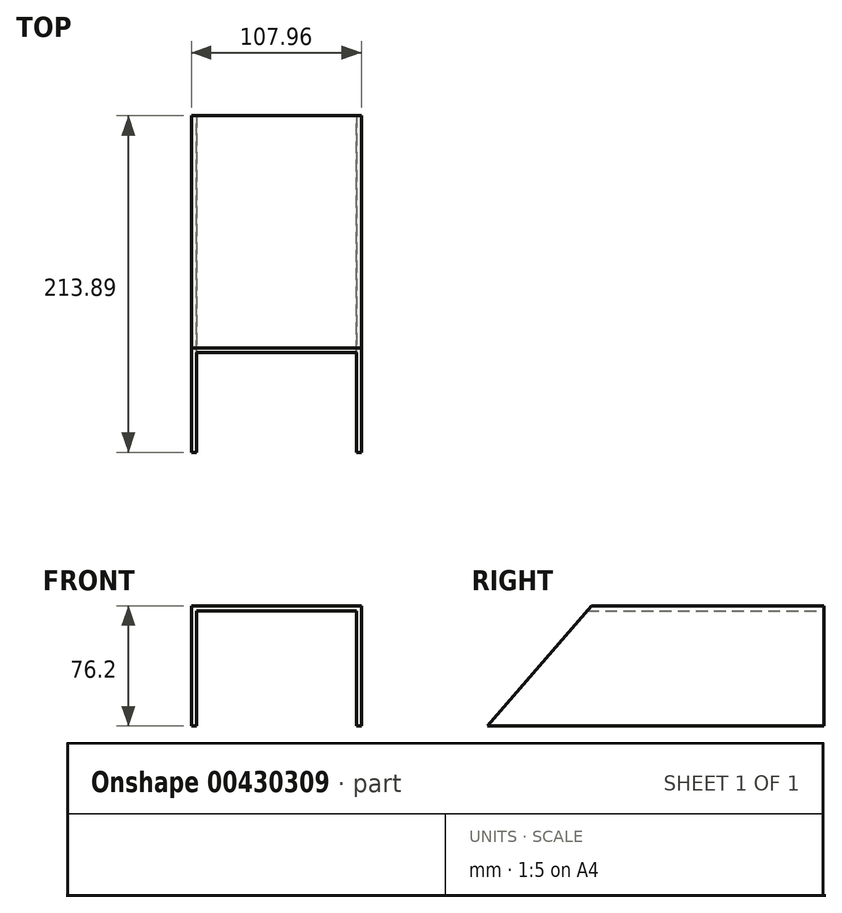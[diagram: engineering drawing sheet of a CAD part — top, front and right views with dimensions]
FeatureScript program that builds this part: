
annotation { "Feature Type Name" : "Feature", "Feature Type Description" : "" }
export const myFeature = defineFeature(function(context is Context, id is Id, definition is map)
    precondition{}
    {
        {
            var Q0;
            Q0=qCreatedBy(makeId("Right.planeOp"),FACE);
            cPlane(context, id + "F0", {"entities" : qUnion([Q0]), "cplaneType" : CPlaneType.OFFSET, "offset" : 50.8 * mm, "width" : 152.4 * mm, "height" : 152.4 * mm});
        }
        {
            var Q0;
            Q0=qCreatedBy(id+"F0.planeOp",FACE);
            var sketch = newSketch(context, id + "F1", { "sketchPlane" : qUnion([Q0])});
            skLineSegment(sketch, "E0", {"start": v(-134.55, 0) * mm, "end": v(-68.29, 76.2) * mm});
            skLineSegment(sketch, "E1", {"start": v(-68.29, 76.2) * mm, "end": v(79.34, 76.2) * mm});
            skLineSegment(sketch, "E2", {"start": v(79.34, 76.2) * mm, "end": v(79.34, 0) * mm});
            skLineSegment(sketch, "E3", {"start": v(79.34, 0) * mm, "end": v(-134.55, 0) * mm});
            skSolve(sketch);
        }
        {
            var Q0;
            Q0=makeQuery(id+"F1.imprint","IMPRINT",FACE,{"disambiguationData":[TD([[makeQuery(id+"F1.imprint","IMPRINT",EDGE,{"derivedFrom":sQuery(id+"F1.wireOp",EDGE,"E0")}),-1.0]])]});
            extrude(context, id + "F2", {"entities" : qUnion([Q0]), "depth" : 3.17 * mm});
        }
        {
            var Q0;
            Q0=makeQuery(id+"F2.opExtrude","SWEPT_BODY",BODY,{"disambiguationData":[OSD([sQuery(id+"F1.wireOp",EDGE,"E0"),sQuery(id+"F1.wireOp",EDGE,"E1"),sQuery(id+"F1.wireOp",EDGE,"E2"),sQuery(id+"F1.wireOp",EDGE,"E3")])]});
            var Q1;
            Q1=qCreatedBy(makeId("Right.planeOp"),FACE);
            mirror(context, id + "F3", {"entities" : qUnion([Q0]), "mirrorPlane" : qUnion([Q1])});
        }
        {
            var Q0;
            Q0=makeQuery(id+"F2.opExtrude","CAP_FACE",FACE,{"disambiguationData":[OSD([sQuery(id+"F1.wireOp",EDGE,"E0"),sQuery(id+"F1.wireOp",EDGE,"E1"),sQuery(id+"F1.wireOp",EDGE,"E2"),sQuery(id+"F1.wireOp",EDGE,"E3")])],"isStart":true});
            var sketch = newSketch(context, id + "F4", { "sketchPlane" : qUnion([Q0])});
            skLineSegment(sketch, "E4", {"start": v(-79.34, 76.2) * mm, "end": v(68.29, 76.2) * mm});
            skLineSegment(sketch, "E5", {"start": v(68.29, 76.2) * mm, "end": v(71.05, 73.03) * mm});
            skLineSegment(sketch, "E6", {"start": v(71.05, 73.03) * mm, "end": v(-79.34, 73.02) * mm});
            skLineSegment(sketch, "E7", {"start": v(-79.34, 73.02) * mm, "end": v(-79.34, 76.2) * mm});
            skSolve(sketch);
        }
        {
            var Q0;
            Q0=makeQuery(id+"F4.imprint","IMPRINT",FACE,{"disambiguationData":[TD([[makeQuery(id+"F4.imprint","IMPRINT",EDGE,{"derivedFrom":sQuery(id+"F4.wireOp",EDGE,"E4")}),1.0]])]});
            extrude(context, id + "F5", {"entities" : qUnion([Q0]), "operationType" : NewBodyOperationType.ADD, "endBound" : BoundingType.UP_TO_NEXT, "depth" : 101.6 * mm});
        }
    });
